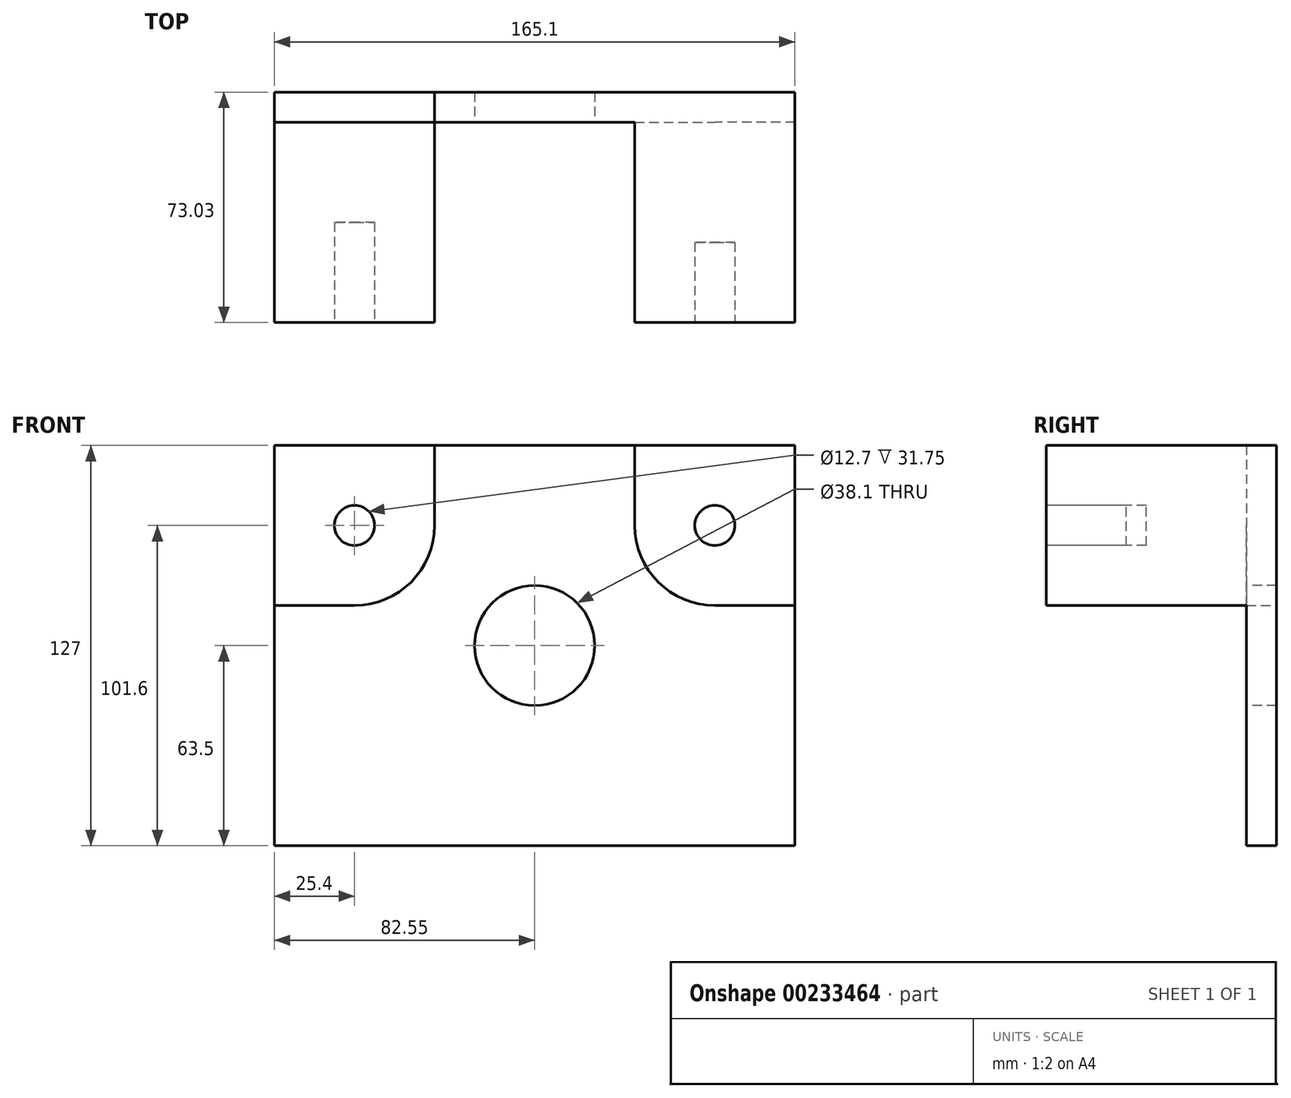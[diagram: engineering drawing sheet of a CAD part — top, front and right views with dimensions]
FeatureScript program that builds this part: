
annotation { "Feature Type Name" : "Feature", "Feature Type Description" : "" }
export const myFeature = defineFeature(function(context is Context, id is Id, definition is map)
    precondition{}
    {
        {
            var Q0;
            Q0=qCreatedBy(makeId("Front.planeOp"),FACE);
            var sketch = newSketch(context, id + "F0", { "sketchPlane" : qUnion([Q0])});
            skLineSegment(sketch, "E0.bottom", {"start": v(-82.55, -63.5) * mm, "end": v(82.55, -63.5) * mm});
            skLineSegment(sketch, "E0.top", {"start": v(-82.55, 63.5) * mm, "end": v(82.55, 63.5) * mm});
            skLineSegment(sketch, "E0.left", {"start": v(-82.55, -63.5) * mm, "end": v(-82.55, 63.5) * mm});
            skLineSegment(sketch, "E0.right", {"start": v(82.55, -63.5) * mm, "end": v(82.55, 63.5) * mm});
            skPoint(sketch, "E0.middle", {"position": v(0, 0) * mm});
            skLineSegment(sketch, "E1.bottom", {"start": v(-82.55, 63.5) * mm, "end": v(-6.35, 63.5) * mm});
            skLineSegment(sketch, "E1.left", {"start": v(-82.55, 63.5) * mm, "end": v(-82.55, 20.3) * mm});
            skLineSegment(sketch, "E2.bottom", {"start": v(82.55, 63.5) * mm, "end": v(34.18, 63.5) * mm});
            skLineSegment(sketch, "E2.left", {"start": v(82.55, 63.5) * mm, "end": v(82.55, 0.8) * mm});
            skPoint(sketch, "E3.visualSharp", {"position": v(-6.35, 20.3) * mm});
            skPoint(sketch, "E4.visualSharp", {"position": v(34.18, 0.8) * mm});
            skLineSegment(sketch, "E5.bottom", {"start": v(-82.55, 63.5) * mm, "end": v(-31.75, 63.5) * mm});
            skLineSegment(sketch, "E5.top", {"start": v(-82.55, 12.7) * mm, "end": v(-57.15, 12.7) * mm});
            skLineSegment(sketch, "E5.left", {"start": v(-82.55, 63.5) * mm, "end": v(-82.55, 12.7) * mm});
            skLineSegment(sketch, "E5.right", {"start": v(-31.75, 63.5) * mm, "end": v(-31.75, 38.1) * mm});
            skLineSegment(sketch, "E6.bottom", {"start": v(82.55, 63.5) * mm, "end": v(31.75, 63.5) * mm});
            skLineSegment(sketch, "E6.top", {"start": v(82.55, 12.7) * mm, "end": v(57.15, 12.7) * mm});
            skLineSegment(sketch, "E6.left", {"start": v(82.55, 63.5) * mm, "end": v(82.55, 12.7) * mm});
            skLineSegment(sketch, "E6.right", {"start": v(31.75, 63.5) * mm, "end": v(31.75, 38.1) * mm});
            skPoint(sketch, "E7.visualSharp", {"position": v(-31.75, 12.7) * mm});
            skArc(sketch, "E7.filletArc", {"start": v(-57.15, 12.7) * mm, "mid": v(-39.19, 20.14) * mm, "end": v(-31.75, 38.1) * mm});
            skPoint(sketch, "E8.visualSharp", {"position": v(31.75, 12.7) * mm});
            skArc(sketch, "E8.filletArc", {"start": v(31.75, 38.1) * mm, "mid": v(39.19, 20.14) * mm, "end": v(57.15, 12.7) * mm});
            skSolve(sketch);
        }
        {
            var Q0;
            Q0=makeQuery(id+"F0.imprint","IMPRINT",FACE,{"disambiguationData":[TD([[makeQuery(id+"F0.imprint","IMPRINT",EDGE,{"derivedFrom":sQuery(id+"F0.wireOp",EDGE,"E0.bottom")}),1.0]])]});
            var Q1;
            {var subQ2=sQuery(id+"F0.wireOp",EDGE,"E5.bottom");Q1=makeQuery(id+"F0.imprint","IMPRINT",FACE,{"disambiguationData":[TD([[makeQuery(id+"F0.imprint","IMPRINT",EDGE,{"derivedFrom":subQ2}),-1.0]])]});}
            var Q2;
            Q2=makeQuery(id+"F0.imprint","IMPRINT",FACE,{"disambiguationData":[TD([[makeQuery(id+"F0.imprint","IMPRINT",EDGE,{"derivedFrom":sQuery(id+"F0.wireOp",EDGE,"E6.top")}),-1.0]])]});
            extrude(context, id + "F1", {"entities" : qUnion([Q0, Q1, Q2]), "depth" : 9.52 * mm});
        }
        {
            var Q0;
            Q0=makeQuery(id+"F1.opExtrude","CAP_FACE",FACE,{"disambiguationData":[OSD([sQuery(id+"F0.wireOp",EDGE,"E0.bottom"),sQuery(id+"F0.wireOp",EDGE,"E0.top"),sQuery(id+"F0.wireOp",EDGE,"E0.left"),sQuery(id+"F0.wireOp",EDGE,"E0.right"),sQuery(id+"F0.wireOp",EDGE,"E1.bottom"),sQuery(id+"F0.wireOp",EDGE,"E2.left"),sQuery(id+"F0.wireOp",EDGE,"E5.bottom"),sQuery(id+"F0.wireOp",EDGE,"E5.left"),sQuery(id+"F0.wireOp",EDGE,"E6.bottom"),sQuery(id+"F0.wireOp",EDGE,"E6.left")])],"isStart":false});
            var sketch = newSketch(context, id + "F2", { "sketchPlane" : qUnion([Q0])});
            skLineSegment(sketch, "E9.bottom", {"start": v(-82.55, 63.5) * mm, "end": v(-31.75, 63.5) * mm});
            skLineSegment(sketch, "E9.top", {"start": v(-82.55, 12.7) * mm, "end": v(-57.15, 12.7) * mm});
            skLineSegment(sketch, "E9.left", {"start": v(-82.55, 63.5) * mm, "end": v(-82.55, 12.7) * mm});
            skLineSegment(sketch, "E9.right", {"start": v(-31.75, 63.5) * mm, "end": v(-31.75, 38.1) * mm});
            skLineSegment(sketch, "E10.bottom", {"start": v(82.55, 63.5) * mm, "end": v(31.75, 63.5) * mm});
            skLineSegment(sketch, "E10.top", {"start": v(82.55, 12.7) * mm, "end": v(57.15, 12.7) * mm});
            skLineSegment(sketch, "E10.left", {"start": v(82.55, 63.5) * mm, "end": v(82.55, 12.7) * mm});
            skLineSegment(sketch, "E10.right", {"start": v(31.75, 63.5) * mm, "end": v(31.75, 38.1) * mm});
            skPoint(sketch, "E11.visualSharp", {"position": v(-31.75, 12.7) * mm});
            skArc(sketch, "E11.filletArc", {"start": v(-57.15, 12.7) * mm, "mid": v(-39.19, 20.14) * mm, "end": v(-31.75, 38.1) * mm});
            skPoint(sketch, "E12.visualSharp", {"position": v(31.75, 12.7) * mm});
            skArc(sketch, "E12.filletArc", {"start": v(31.75, 38.1) * mm, "mid": v(39.19, 20.14) * mm, "end": v(57.15, 12.7) * mm});
            skSolve(sketch);
        }
        {
            var Q0;
            Q0 = qSketchRegion(id + "F2", true);
            extrude(context, id + "F3", {"entities" : qUnion([Q0]), "operationType" : NewBodyOperationType.ADD, "depth" : 63.5 * mm});
        }
        {
            var Q0;
            Q0=makeQuery(id+"F1.opExtrude","CAP_FACE",FACE,{"disambiguationData":[OSD([sQuery(id+"F0.wireOp",EDGE,"E0.bottom"),sQuery(id+"F0.wireOp",EDGE,"E0.top"),sQuery(id+"F0.wireOp",EDGE,"E0.left"),sQuery(id+"F0.wireOp",EDGE,"E0.right"),sQuery(id+"F0.wireOp",EDGE,"E1.bottom"),sQuery(id+"F0.wireOp",EDGE,"E2.left"),sQuery(id+"F0.wireOp",EDGE,"E5.bottom"),sQuery(id+"F0.wireOp",EDGE,"E5.left"),sQuery(id+"F0.wireOp",EDGE,"E6.bottom"),sQuery(id+"F0.wireOp",EDGE,"E6.left")])],"isStart":false});
            var sketch = newSketch(context, id + "F4", { "sketchPlane" : qUnion([Q0])});
            skCircle(sketch, "E13", {"center": v(0, 0) * mm, "radius": 19.05 * mm});
            skSolve(sketch);
        }
        {
            var Q0;
            Q0=makeQuery(id+"F4.imprint","IMPRINT",FACE,{"disambiguationData":[TD([[makeQuery(id+"F4.imprint","IMPRINT",EDGE,{"derivedFrom":sQuery(id+"F4.wireOp",EDGE,"E13")}),1.0]])]});
            var Q1;
            Q1=sQuery(id+"F4.wireOp",EDGE,"E13");
            extrude(context, id + "F5", {"entities" : qUnion([Q0]), "operationType" : NewBodyOperationType.REMOVE, "surfaceEntities" : qUnion([Q1]), "endBound" : BoundingType.THROUGH_ALL, "oppositeDirection" : true, "depth" : 25.4 * mm});
        }
        {
            var Q0;
            Q0=makeQuery(id+"F3.opExtrude","CAP_FACE",FACE,{"disambiguationData":[OSD([sQuery(id+"F2.wireOp",EDGE,"E9.bottom"),sQuery(id+"F2.wireOp",EDGE,"E9.top"),sQuery(id+"F2.wireOp",EDGE,"E9.left"),sQuery(id+"F2.wireOp",EDGE,"E9.right"),sQuery(id+"F2.wireOp",EDGE,"E11.filletArc")])],"isStart":false});
            var sketch = newSketch(context, id + "F6", { "sketchPlane" : qUnion([Q0])});
            skCircle(sketch, "E14", {"center": v(-57.15, 38.1) * mm, "radius": 6.35 * mm});
            skSolve(sketch);
        }
        {
            var Q0;
            Q0=makeQuery(id+"F6.imprint","IMPRINT",FACE,{"disambiguationData":[TD([[makeQuery(id+"F6.imprint","IMPRINT",EDGE,{"derivedFrom":sQuery(id+"F6.wireOp",EDGE,"E14")}),1.0]])]});
            extrude(context, id + "F7", {"entities" : qUnion([Q0]), "operationType" : NewBodyOperationType.REMOVE, "oppositeDirection" : true, "depth" : 31.75 * mm});
        }
        {
            var Q0;
            Q0 = qSketchRegion(id + "F6", true);
            extrude(context, id + "F8", {"entities" : qUnion([Q0]), "operationType" : NewBodyOperationType.REMOVE, "oppositeDirection" : true, "depth" : 25.4 * mm});
        }
        {
            var Q0;
            Q0=makeQuery(id+"F3.opExtrude","CAP_FACE",FACE,{"disambiguationData":[OSD([sQuery(id+"F2.wireOp",EDGE,"E10.bottom"),sQuery(id+"F2.wireOp",EDGE,"E10.top"),sQuery(id+"F2.wireOp",EDGE,"E10.left"),sQuery(id+"F2.wireOp",EDGE,"E10.right"),sQuery(id+"F2.wireOp",EDGE,"E12.filletArc")])],"isStart":false});
            var sketch = newSketch(context, id + "F9", { "sketchPlane" : qUnion([Q0])});
            skCircle(sketch, "E15", {"center": v(57.15, 38.1) * mm, "radius": 6.35 * mm});
            skSolve(sketch);
        }
        {
            var Q0;
            Q0 = qSketchRegion(id + "F9", true);
            extrude(context, id + "F10", {"entities" : qUnion([Q0]), "operationType" : NewBodyOperationType.REMOVE, "oppositeDirection" : true, "depth" : 25.4 * mm});
        }
    });
